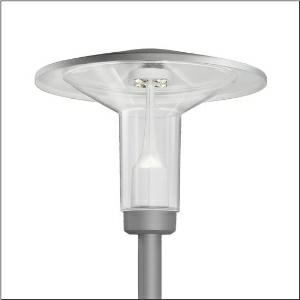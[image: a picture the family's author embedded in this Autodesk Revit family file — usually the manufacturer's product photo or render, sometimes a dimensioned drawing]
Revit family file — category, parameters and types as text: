
# Revit family: laterne_iq___pl1_2s_5xa5255rf14h_c5ef
name_source: partatom
category: Lighting Fixtures
units: mm (PartAtom-declared; Revit-internal decimal feet)

## family parameters
Cut with Voids When Loaded = No
Host = Face
Light Source = No
Part Type = Normal
Room Calculation Point = No
Round Connector Dimension = Use Diameter
Shared = No

## types (1)
- --- (1 x LED, 2970 lm, 18.5 W, 4000K)
    Apparent Load = 19 VA
    CIE Flux Codes = 25 63 94 98 100
    Color Rendering = 70
    Color Temperature = 4000K
    Default Elevation = 1800 mm
    Description = Lantern iQ, mast luminaire, Module 540 iQ-SR, primary light control with 3 zone facetted reflector, of plastic, silver coated, highly specular, structured, primary optical cover: cover, of PMMA, transparent, light distribution: PL1.2s, light emission: direct distribution, primary light characteristic: symmetric, installation type: post-top, LED, High Power LED, rated luminous flux: 2.970lm, luminous efficacy: 161lm/W, light colour: 740, colour temperature: 4000K, control gear: iQ Street-Remote, control: pre-setting: logarithmic dimming characteristic, Street-Remote, Auto-Match, Temp-Guard, Lumen-Switch, Night-Set, Smart-Wire, Light-Fading, Desk-Remote (wireless, voltage-free reading and setting of iQ features in the workshop via application-optimized NFC function/RFID function), optimised constant luminous flux control (CLO 2.0), with terminal, 6-pole, max. 2.5mm², mains connection: 230..240V, AC, 50/60Hz, start of lifetime: 19W, end of service life: 20W, reduction: 9W, luminaire housing, upper part, of glass-fibre reinforced polyester, coated, Siteco® metallic grey (DB 702S), diameter: 750mm, height: 583mm, spigot size: d x l = 76 x 70mm (post-top) | with reducer (optional accessory) 60 x 70mm, mounting height: 3..5m, post-top mast mounting element, of diecast aluminium, coated, Siteco® metallic grey (DB 702S), Module 540 iQ-SR, traffic white (RAL 9016), equipment: standard, protection rating (complete): IP65, insulation class (complete): insulation class II (safety insulation), certification: CE, ENEC, VDE, packaging unit: 1 piece

Light Distribution: PL1.2s
    Height = 583 mm
    Lamp = 1 x LED
    Lamp Light Flux = 2970 lm
    Lamp Power = 18.5 W
    Lamp count = 1
    Length = 750 mm
    Luminous efficacy = 161 lm/W
    Manufacturer = Siteco
    ModVariant = No
    Model = 5XA5255RF14H
    Number of Poles = 1
    OnlyDefault = Yes
    Power Factor = 1
    Product Name = Laterne iQ | PL1.2s
    Product group = mast luminaire | pylon top
    ProductGroupID = 6100
    Protection Class = Protection class II
    Protection Degree = IP 65
    RLX_Detail_Level = 1
    RLX_Emergency_Light_Flux = 0 lm
    RLX_Emergency_Type = 0
    RLX_Emergency_Type_DB = No
    RlxData = <blob elided: 31665 chars, md5=7b7295b6>
    Socket = socket
    Standby Power = 0 W
    System Light Flux = 2970 lm
    System Power = 19 W
    Type Comments = factory setting: luminous flux: 100 % | dim-lin: 254 | 385 mA
    Type Image = l_1006050.jpg
    URL = http://relux.com
    VarID = @adj_145886
    Voltage = 0 V
    Weight = 0.00 kg
    Width = 0 mm  [stored 0 ft]

note: [stored X ft] marks values corroborated as IEEE doubles in the binary element streams (Revit-internal decimal feet)

## geometry (parser evidence)
native form markers: Blend x4, Sweep x9
no freeform markers — native parametric forms only
